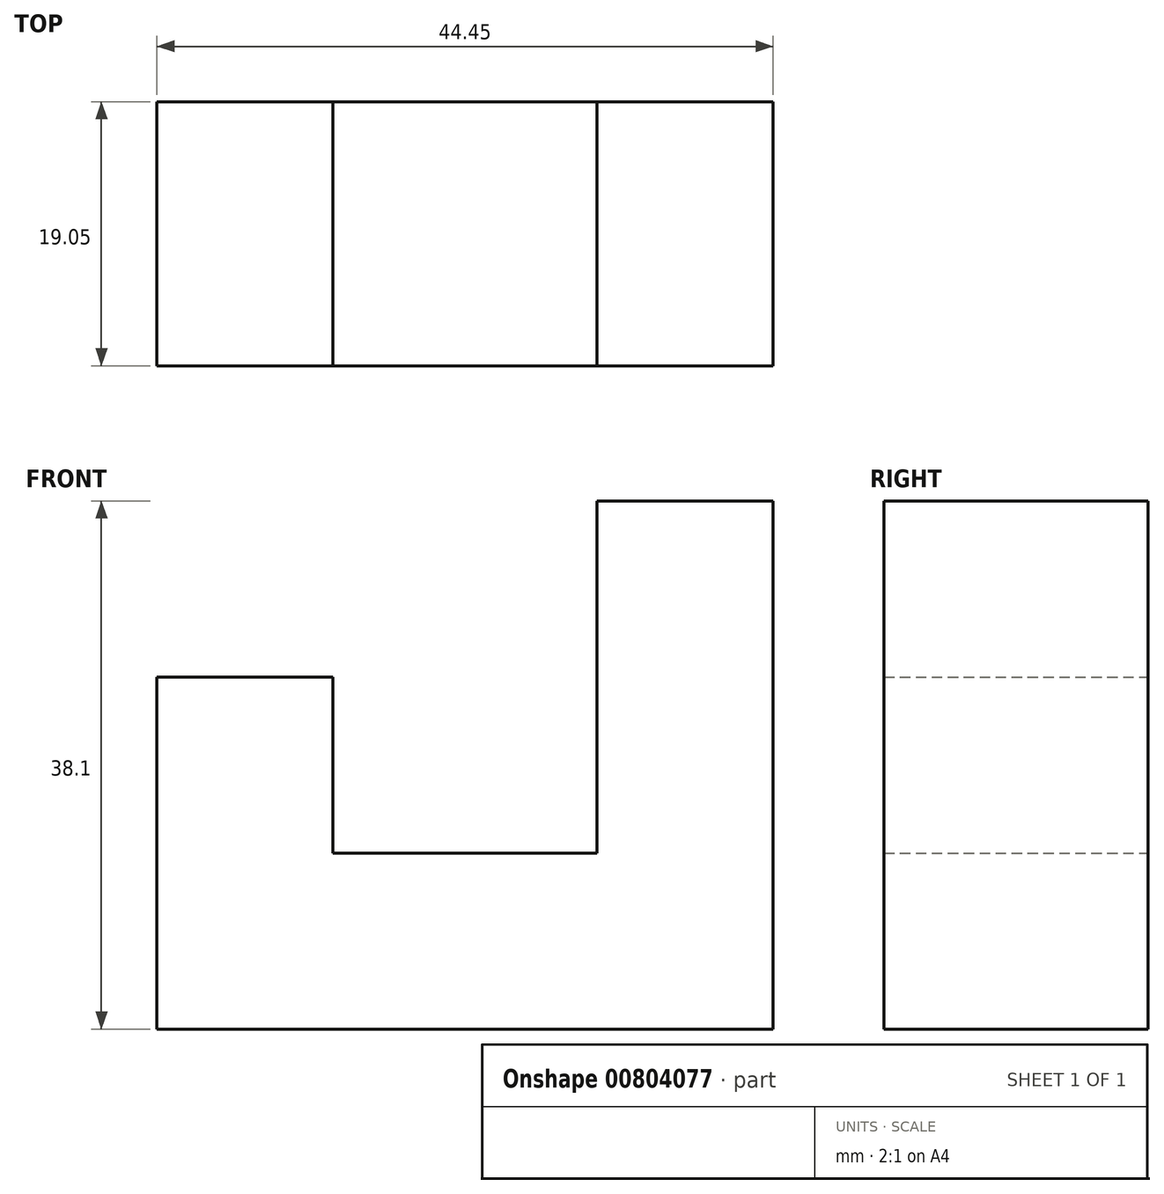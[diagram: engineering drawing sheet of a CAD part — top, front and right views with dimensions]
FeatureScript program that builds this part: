
annotation { "Feature Type Name" : "Feature", "Feature Type Description" : "" }
export const myFeature = defineFeature(function(context is Context, id is Id, definition is map)
    precondition{}
    {
        {
            var Q0;
            Q0=qCreatedBy(makeId("Front.planeOp"),FACE);
            var sketch = newSketch(context, id + "F0", { "sketchPlane" : qUnion([Q0])});
            skLineSegment(sketch, "E0", {"start": v(0, 0) * mm, "end": v(44.45, 0) * mm});
            skLineSegment(sketch, "E1", {"start": v(44.45, 0) * mm, "end": v(44.45, 38.1) * mm});
            skLineSegment(sketch, "E2", {"start": v(44.45, 38.1) * mm, "end": v(31.75, 38.1) * mm});
            skLineSegment(sketch, "E3", {"start": v(31.75, 38.1) * mm, "end": v(31.75, 12.7) * mm});
            skLineSegment(sketch, "E4", {"start": v(31.75, 12.7) * mm, "end": v(12.7, 12.7) * mm});
            skLineSegment(sketch, "E5", {"start": v(12.7, 12.7) * mm, "end": v(12.7, 25.4) * mm});
            skLineSegment(sketch, "E6", {"start": v(12.7, 25.4) * mm, "end": v(0, 25.4) * mm});
            skLineSegment(sketch, "E7", {"start": v(0, 25.4) * mm, "end": v(0, 0) * mm});
            skSolve(sketch);
        }
        {
            var Q0;
            Q0 = qSketchRegion(id + "F0", true);
            extrude(context, id + "F1", {"entities" : qUnion([Q0]), "depth" : 19.05 * mm, "offsetDistance" : 25.4 * mm});
        }
    });
